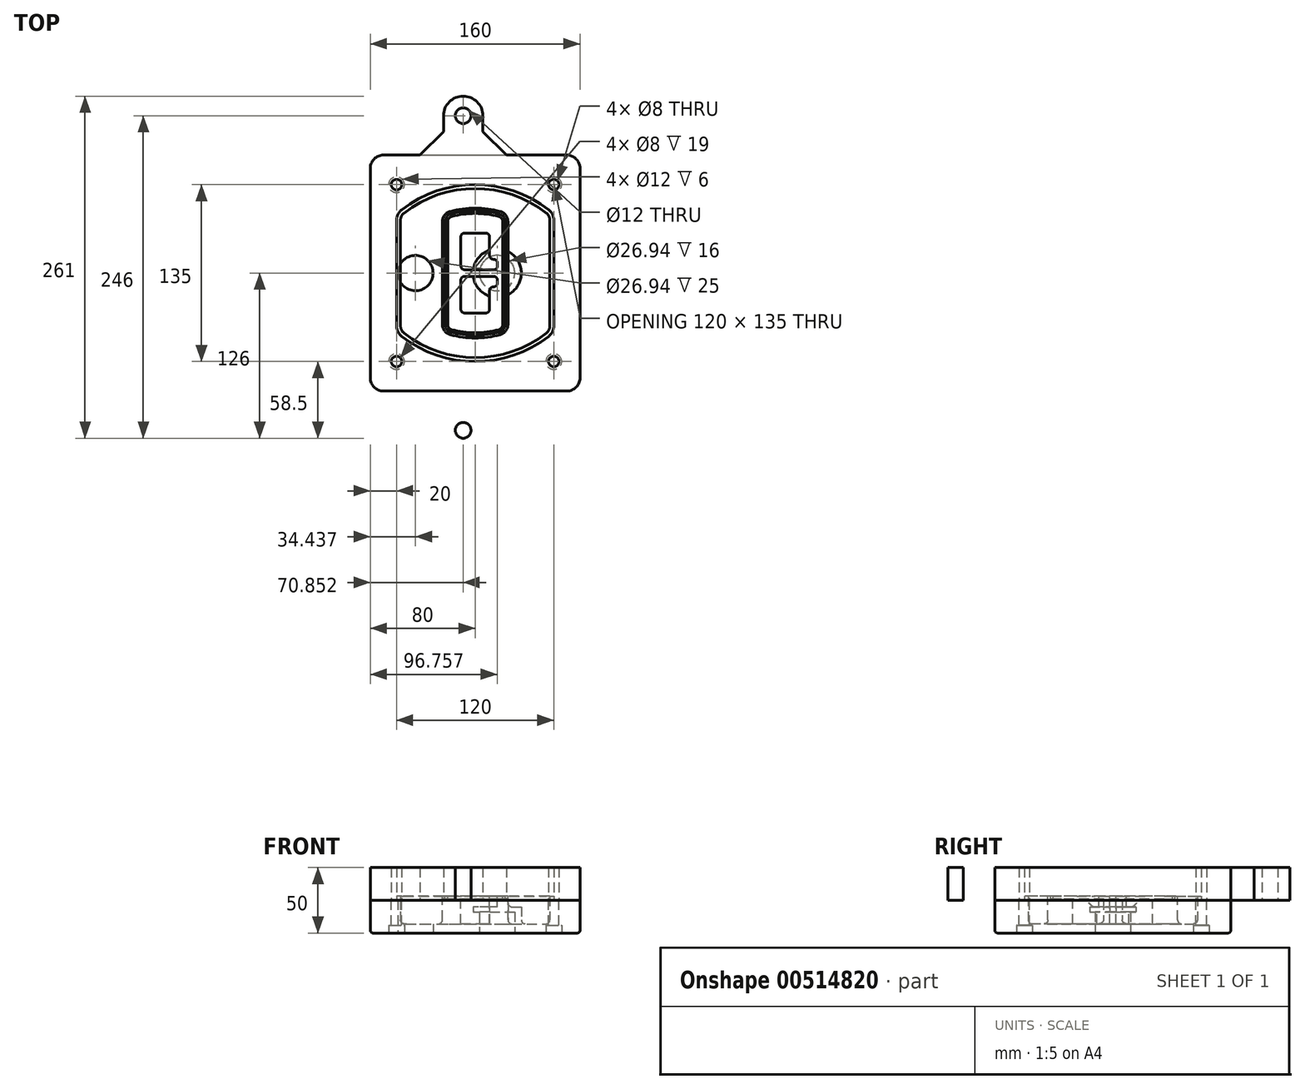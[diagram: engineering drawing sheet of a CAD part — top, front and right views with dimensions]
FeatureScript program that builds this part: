
annotation { "Feature Type Name" : "Feature", "Feature Type Description" : "" }
export const myFeature = defineFeature(function(context is Context, id is Id, definition is map)
    precondition{}
    {
        {
            var Q0;
            Q0=qCreatedBy(makeId("Top.planeOp"),FACE);
            var sketch = newSketch(context, id + "F0", { "sketchPlane" : qUnion([Q0])});
            skPoint(sketch, "E0.rect.middle", {"position": v(0, 0) * mm});
            skLineSegment(sketch, "E1.bottom", {"start": v(-70, -90) * mm, "end": v(70, -90) * mm});
            skLineSegment(sketch, "E1.top", {"start": v(-70, 90) * mm, "end": v(70, 90) * mm});
            skLineSegment(sketch, "E1.left", {"start": v(-80, -80) * mm, "end": v(-80, 80) * mm});
            skLineSegment(sketch, "E1.right", {"start": v(80, -80) * mm, "end": v(80, 80) * mm});
            skLineSegment(sketch, "E2", {"start": v(-80, 90) * mm, "end": v(80, -90) * mm, "construction": true});
            skLineSegment(sketch, "E3", {"start": v(80, 90) * mm, "end": v(-80, -90) * mm, "construction": true});
            skCircle(sketch, "E4", {"center": v(-60, 67.5) * mm, "radius": 4 * mm});
            skCircle(sketch, "E5", {"center": v(60, 67.5) * mm, "radius": 4 * mm});
            skCircle(sketch, "E6", {"center": v(60, -67.5) * mm, "radius": 4 * mm});
            skCircle(sketch, "E7", {"center": v(-60, -67.5) * mm, "radius": 4 * mm});
            skLineSegment(sketch, "E8", {"start": v(-60, 67.5) * mm, "end": v(60, 67.5) * mm, "construction": true});
            skLineSegment(sketch, "E9", {"start": v(60, 67.5) * mm, "end": v(60, -67.5) * mm, "construction": true});
            skLineSegment(sketch, "E10", {"start": v(60, -67.5) * mm, "end": v(-60, -67.5) * mm, "construction": true});
            skLineSegment(sketch, "E11", {"start": v(-60, -67.5) * mm, "end": v(-60, 67.5) * mm, "construction": true});
            skLineSegment(sketch, "E12", {"start": v(-60, 40.3) * mm, "end": v(-60, -40.3) * mm});
            skLineSegment(sketch, "E13", {"start": v(60, 40.3) * mm, "end": v(60, -40.3) * mm});
            skArc(sketch, "E14", {"start": v(56.15, 48.18) * mm, "mid": v(0, 67.5) * mm, "end": v(-56.15, 48.18) * mm});
            skArc(sketch, "E15", {"start": v(-56.15, -48.18) * mm, "mid": v(0, -67.5) * mm, "end": v(56.15, -48.18) * mm});
            skLineSegment(sketch, "E16", {"start": v(-60, 0) * mm, "end": v(60, 0) * mm, "construction": true});
            skPoint(sketch, "E17.visualSharp", {"position": v(-60, -45) * mm});
            skArc(sketch, "E17.filletArc", {"start": v(-60, -40.3) * mm, "mid": v(-58.99, -44.68) * mm, "end": v(-56.15, -48.18) * mm});
            skPoint(sketch, "E18.visualSharp", {"position": v(-60, 45) * mm});
            skArc(sketch, "E18.filletArc", {"start": v(-56.15, 48.18) * mm, "mid": v(-58.99, 44.68) * mm, "end": v(-60, 40.3) * mm});
            skPoint(sketch, "E19.visualSharp", {"position": v(60, 45) * mm});
            skArc(sketch, "E19.filletArc", {"start": v(60, 40.3) * mm, "mid": v(58.99, 44.68) * mm, "end": v(56.15, 48.18) * mm});
            skPoint(sketch, "E20.visualSharp", {"position": v(60, -45) * mm});
            skArc(sketch, "E20.filletArc", {"start": v(56.15, -48.18) * mm, "mid": v(58.99, -44.68) * mm, "end": v(60, -40.3) * mm});
            skPoint(sketch, "E21.visualSharp", {"position": v(-80, 90) * mm});
            skArc(sketch, "E21.filletArc", {"start": v(-70, 90) * mm, "mid": v(-77.07, 87.07) * mm, "end": v(-80, 80) * mm});
            skPoint(sketch, "E22.visualSharp", {"position": v(80, 90) * mm});
            skArc(sketch, "E22.filletArc", {"start": v(80, 80) * mm, "mid": v(77.07, 87.07) * mm, "end": v(70, 90) * mm});
            skPoint(sketch, "E23.visualSharp", {"position": v(80, -90) * mm});
            skArc(sketch, "E23.filletArc", {"start": v(70, -90) * mm, "mid": v(77.07, -87.07) * mm, "end": v(80, -80) * mm});
            skPoint(sketch, "E24.visualSharp", {"position": v(-80, -90) * mm});
            skArc(sketch, "E24.filletArc", {"start": v(-80, -80) * mm, "mid": v(-77.07, -87.07) * mm, "end": v(-70, -90) * mm});
            skArc(sketch, "E25.0", {"start": v(57, 40.3) * mm, "mid": v(56.3, 43.36) * mm, "end": v(54.3, 45.81) * mm});
            skLineSegment(sketch, "E25.1", {"start": v(57, 40.3) * mm, "end": v(57, -40.3) * mm});
            skArc(sketch, "E25.2", {"start": v(54.3, -45.81) * mm, "mid": v(56.3, -43.36) * mm, "end": v(57, -40.3) * mm});
            skArc(sketch, "E25.3", {"start": v(-54.3, -45.81) * mm, "mid": v(0, -64.5) * mm, "end": v(54.3, -45.81) * mm});
            skArc(sketch, "E25.4", {"start": v(-57, -40.3) * mm, "mid": v(-56.3, -43.36) * mm, "end": v(-54.3, -45.81) * mm});
            skArc(sketch, "E25.5", {"start": v(54.3, 45.81) * mm, "mid": v(0, 64.5) * mm, "end": v(-54.3, 45.81) * mm});
            skLineSegment(sketch, "E25.6", {"start": v(-57, 40.3) * mm, "end": v(-57, -40.3) * mm});
            skArc(sketch, "E25.7", {"start": v(-54.3, 45.81) * mm, "mid": v(-56.3, 43.36) * mm, "end": v(-57, 40.3) * mm});
            skArc(sketch, "E26.0", {"start": v(-58.62, 51.33) * mm, "mid": v(-62.58, 46.43) * mm, "end": v(-64, 40.3) * mm});
            skArc(sketch, "E26.1", {"start": v(58.62, 51.33) * mm, "mid": v(0, 71.5) * mm, "end": v(-58.62, 51.33) * mm});
            skArc(sketch, "E26.2", {"start": v(64, 40.3) * mm, "mid": v(62.58, 46.43) * mm, "end": v(58.62, 51.33) * mm});
            skLineSegment(sketch, "E26.3", {"start": v(64, 40.3) * mm, "end": v(64, -40.3) * mm});
            skArc(sketch, "E26.4", {"start": v(58.62, -51.33) * mm, "mid": v(62.58, -46.43) * mm, "end": v(64, -40.3) * mm});
            skLineSegment(sketch, "E26.5", {"start": v(-64, 40.3) * mm, "end": v(-64, -40.3) * mm});
            skArc(sketch, "E26.6", {"start": v(-58.62, -51.33) * mm, "mid": v(0, -71.5) * mm, "end": v(58.62, -51.33) * mm});
            skArc(sketch, "E26.7", {"start": v(-64, -40.3) * mm, "mid": v(-62.58, -46.43) * mm, "end": v(-58.62, -51.33) * mm});
            skSolve(sketch);
        }
        {
            var Q0;
            Q0=makeQuery(id+"F0.imprint","IMPRINT",FACE,{"disambiguationData":[TD([[makeQuery(id+"F0.imprint","IMPRINT",EDGE,{"derivedFrom":sQuery(id+"F0.wireOp",EDGE,"E1.bottom")}),1.0]])]});
            var Q1;
            Q1=makeQuery(id+"F0.imprint","IMPRINT",FACE,{"disambiguationData":[TD([[makeQuery(id+"F0.imprint","IMPRINT",EDGE,{"derivedFrom":sQuery(id+"F0.wireOp",EDGE,"E12")}),1.0]])]});
            var Q2;
            Q2=makeQuery(id+"F0.imprint","IMPRINT",FACE,{"disambiguationData":[TD([[makeQuery(id+"F0.imprint","IMPRINT",EDGE,{"derivedFrom":sQuery(id+"F0.wireOp",EDGE,"E25.0")}),1.0]])]});
            var Q3;
            Q3=makeQuery(id+"F0.imprint","IMPRINT",FACE,{"disambiguationData":[TD([[makeQuery(id+"F0.imprint","IMPRINT",EDGE,{"derivedFrom":sQuery(id+"F0.wireOp",EDGE,"E12")}),-1.0]])]});
            extrude(context, id + "F1", {"entities" : qUnion([Q0, Q1, Q2, Q3]), "oppositeDirection" : true, "depth" : 25 * mm});
        }
        {
            var Q0;
            Q0=makeQuery(id+"F0.imprint","IMPRINT",FACE,{"disambiguationData":[TD([[makeQuery(id+"F0.imprint","IMPRINT",EDGE,{"derivedFrom":sQuery(id+"F0.wireOp",EDGE,"E12")}),1.0]])]});
            extrude(context, id + "F2", {"entities" : qUnion([Q0]), "operationType" : NewBodyOperationType.ADD, "depth" : 3 * mm});
        }
        {
            var Q0;
            Q0=makeQuery(id+"F0.imprint","IMPRINT",FACE,{"disambiguationData":[TD([[makeQuery(id+"F0.imprint","IMPRINT",EDGE,{"derivedFrom":sQuery(id+"F0.wireOp",EDGE,"E25.0")}),1.0]])]});
            extrude(context, id + "F3", {"entities" : qUnion([Q0]), "operationType" : NewBodyOperationType.REMOVE, "oppositeDirection" : true, "depth" : 18 * mm});
        }
        {
            var Q0;
            Q0=makeQuery(id+"F2.opExtrude","CAP_FACE",FACE,{"disambiguationData":[OSD([sQuery(id+"F0.wireOp",EDGE,"E12"),sQuery(id+"F0.wireOp",EDGE,"E13"),sQuery(id+"F0.wireOp",EDGE,"E14"),sQuery(id+"F0.wireOp",EDGE,"E15"),sQuery(id+"F0.wireOp",EDGE,"E17.filletArc"),sQuery(id+"F0.wireOp",EDGE,"E18.filletArc"),sQuery(id+"F0.wireOp",EDGE,"E19.filletArc"),sQuery(id+"F0.wireOp",EDGE,"E20.filletArc"),sQuery(id+"F0.wireOp",EDGE,"E25.0"),sQuery(id+"F0.wireOp",EDGE,"E25.1"),sQuery(id+"F0.wireOp",EDGE,"E25.2"),sQuery(id+"F0.wireOp",EDGE,"E25.3"),sQuery(id+"F0.wireOp",EDGE,"E25.4"),sQuery(id+"F0.wireOp",EDGE,"E25.5"),sQuery(id+"F0.wireOp",EDGE,"E25.6"),sQuery(id+"F0.wireOp",EDGE,"E25.7")])],"isStart":false});
            var sketch = newSketch(context, id + "F4", { "sketchPlane" : qUnion([Q0])});
            skArc(sketch, "E27.0", {"start": v(-19.08, -46.97) * mm, "mid": v(0, -49.5) * mm, "end": v(19.08, -46.97) * mm});
            skArc(sketch, "E28.0", {"start": v(19.08, 46.97) * mm, "mid": v(0, 49.5) * mm, "end": v(-19.08, 46.97) * mm});
            skLineSegment(sketch, "E29", {"start": v(-25, 39.25) * mm, "end": v(-25, -39.25) * mm});
            skLineSegment(sketch, "E30", {"start": v(25, 39.25) * mm, "end": v(25, -39.25) * mm});
            skLineSegment(sketch, "E31", {"start": v(-25, 45.1) * mm, "end": v(25, 45.1) * mm, "construction": true});
            skLineSegment(sketch, "E32", {"start": v(-25, -45.1) * mm, "end": v(25, -45.1) * mm, "construction": true});
            skPoint(sketch, "E33.visualSharp", {"position": v(-25, 45.1) * mm});
            skArc(sketch, "E33.filletArc", {"start": v(-19.08, 46.97) * mm, "mid": v(-23.35, 44.11) * mm, "end": v(-25, 39.25) * mm});
            skPoint(sketch, "E34.visualSharp", {"position": v(25, 45.1) * mm});
            skArc(sketch, "E34.filletArc", {"start": v(25, 39.25) * mm, "mid": v(23.35, 44.11) * mm, "end": v(19.08, 46.97) * mm});
            skPoint(sketch, "E35.visualSharp", {"position": v(25, -45.1) * mm});
            skArc(sketch, "E35.filletArc", {"start": v(19.08, -46.97) * mm, "mid": v(23.35, -44.11) * mm, "end": v(25, -39.25) * mm});
            skPoint(sketch, "E36.visualSharp", {"position": v(-25, -45.1) * mm});
            skArc(sketch, "E36.filletArc", {"start": v(-25, -39.25) * mm, "mid": v(-23.35, -44.11) * mm, "end": v(-19.08, -46.97) * mm});
            skArc(sketch, "E37.0", {"start": v(54.3, 45.81) * mm, "mid": v(0, 64.5) * mm, "end": v(-54.3, 45.81) * mm});
            skArc(sketch, "E37.1", {"start": v(-54.3, 45.81) * mm, "mid": v(-56.3, 43.36) * mm, "end": v(-57, 40.3) * mm});
            skLineSegment(sketch, "E37.2", {"start": v(-57, 40.3) * mm, "end": v(-57, -40.3) * mm});
            skArc(sketch, "E37.3", {"start": v(-57, -40.3) * mm, "mid": v(-56.3, -43.36) * mm, "end": v(-54.3, -45.81) * mm});
            skArc(sketch, "E37.4", {"start": v(-54.3, -45.81) * mm, "mid": v(0, -64.5) * mm, "end": v(54.3, -45.81) * mm});
            skArc(sketch, "E37.5", {"start": v(54.3, -45.81) * mm, "mid": v(56.3, -43.36) * mm, "end": v(57, -40.3) * mm});
            skLineSegment(sketch, "E37.6", {"start": v(57, 40.3) * mm, "end": v(57, -40.3) * mm});
            skArc(sketch, "E37.7", {"start": v(57, 40.3) * mm, "mid": v(56.3, 43.36) * mm, "end": v(54.3, 45.81) * mm});
            skLineSegment(sketch, "E38.0", {"start": v(23, 39.25) * mm, "end": v(23, -39.25) * mm});
            skArc(sketch, "E38.1", {"start": v(18.56, -45.04) * mm, "mid": v(21.76, -42.9) * mm, "end": v(23, -39.25) * mm});
            skArc(sketch, "E38.2", {"start": v(-18.56, -45.04) * mm, "mid": v(0, -47.5) * mm, "end": v(18.56, -45.04) * mm});
            skArc(sketch, "E38.3", {"start": v(-23, -39.25) * mm, "mid": v(-21.76, -42.9) * mm, "end": v(-18.56, -45.04) * mm});
            skLineSegment(sketch, "E38.4", {"start": v(-23, 39.25) * mm, "end": v(-23, -39.25) * mm});
            skArc(sketch, "E38.5", {"start": v(23, 39.25) * mm, "mid": v(21.76, 42.9) * mm, "end": v(18.56, 45.04) * mm});
            skArc(sketch, "E38.6", {"start": v(-18.56, 45.04) * mm, "mid": v(-21.76, 42.9) * mm, "end": v(-23, 39.25) * mm});
            skArc(sketch, "E38.7", {"start": v(18.56, 45.04) * mm, "mid": v(0, 47.5) * mm, "end": v(-18.56, 45.04) * mm});
            skArc(sketch, "E39.0", {"start": v(21, 39.25) * mm, "mid": v(20.18, 41.68) * mm, "end": v(18.04, 43.1) * mm});
            skLineSegment(sketch, "E39.1", {"start": v(21, 39.25) * mm, "end": v(21, -39.25) * mm});
            skArc(sketch, "E39.2", {"start": v(18.04, -43.1) * mm, "mid": v(20.18, -41.68) * mm, "end": v(21, -39.25) * mm});
            skArc(sketch, "E39.3", {"start": v(-18.04, -43.1) * mm, "mid": v(0, -45.5) * mm, "end": v(18.04, -43.1) * mm});
            skArc(sketch, "E39.4", {"start": v(-21, -39.25) * mm, "mid": v(-20.18, -41.68) * mm, "end": v(-18.04, -43.1) * mm});
            skArc(sketch, "E39.5", {"start": v(18.04, 43.1) * mm, "mid": v(0, 45.5) * mm, "end": v(-18.04, 43.1) * mm});
            skLineSegment(sketch, "E39.6", {"start": v(-21, 39.25) * mm, "end": v(-21, -39.25) * mm});
            skArc(sketch, "E39.7", {"start": v(-18.04, 43.1) * mm, "mid": v(-20.18, 41.68) * mm, "end": v(-21, 39.25) * mm});
            skLineSegment(sketch, "E40", {"start": v(-25, 0) * mm, "end": v(25, 0) * mm, "construction": true});
            skLineSegment(sketch, "E41", {"start": v(-11, 5.5) * mm, "end": v(-11, 27.5) * mm});
            skLineSegment(sketch, "E42", {"start": v(-8, 30.5) * mm, "end": v(8, 30.5) * mm});
            skLineSegment(sketch, "E43", {"start": v(11, 27.5) * mm, "end": v(11, 13.5) * mm});
            skLineSegment(sketch, "E44", {"start": v(14, 10.5) * mm, "end": v(14, 10.5) * mm});
            skLineSegment(sketch, "E45", {"start": v(17, 7.5) * mm, "end": v(17, 5.5) * mm});
            skLineSegment(sketch, "E46", {"start": v(14, 2.5) * mm, "end": v(-8, 2.5) * mm});
            skPoint(sketch, "E47.visualSharp", {"position": v(-11, 30.5) * mm});
            skArc(sketch, "E47.filletArc", {"start": v(-8, 30.5) * mm, "mid": v(-10.12, 29.62) * mm, "end": v(-11, 27.5) * mm});
            skPoint(sketch, "E48.visualSharp", {"position": v(11, 30.5) * mm});
            skArc(sketch, "E48.filletArc", {"start": v(11, 27.5) * mm, "mid": v(10.12, 29.62) * mm, "end": v(8, 30.5) * mm});
            skPoint(sketch, "E49.visualSharp", {"position": v(11, 10.5) * mm});
            skArc(sketch, "E49.filletArc", {"start": v(11, 13.5) * mm, "mid": v(11.88, 11.38) * mm, "end": v(14, 10.5) * mm});
            skPoint(sketch, "E50.visualSharp", {"position": v(17, 10.5) * mm});
            skArc(sketch, "E50.filletArc", {"start": v(17, 7.5) * mm, "mid": v(16.12, 9.62) * mm, "end": v(14, 10.5) * mm});
            skPoint(sketch, "E51.visualSharp", {"position": v(17, 2.5) * mm});
            skArc(sketch, "E51.filletArc", {"start": v(14, 2.5) * mm, "mid": v(16.12, 3.38) * mm, "end": v(17, 5.5) * mm});
            skPoint(sketch, "E52.visualSharp", {"position": v(-11, 2.5) * mm});
            skArc(sketch, "E52.filletArc", {"start": v(-11, 5.5) * mm, "mid": v(-10.12, 3.38) * mm, "end": v(-8, 2.5) * mm});
            skLineSegment(sketch, "E53.0.MirrorCS", {"start": v(14, -2.5) * mm, "end": v(-8, -2.5) * mm});
            skArc(sketch, "E54.0.MirrorCS", {"start": v(-11, -5.5) * mm, "mid": v(-10.12, -3.38) * mm, "end": v(-8, -2.5) * mm});
            skLineSegment(sketch, "E55.0.MirrorCS", {"start": v(-11, -5.5) * mm, "end": v(-11, -27.5) * mm});
            skArc(sketch, "E56.0.MirrorCS", {"start": v(-8, -30.5) * mm, "mid": v(-10.12, -29.62) * mm, "end": v(-11, -27.5) * mm});
            skLineSegment(sketch, "E57.0.MirrorCS", {"start": v(-8, -30.5) * mm, "end": v(8, -30.5) * mm});
            skArc(sketch, "E58.0.MirrorCS", {"start": v(11, -27.5) * mm, "mid": v(10.12, -29.62) * mm, "end": v(8, -30.5) * mm});
            skLineSegment(sketch, "E59.0.MirrorCS", {"start": v(11, -27.5) * mm, "end": v(11, -13.5) * mm});
            skArc(sketch, "E60.0.MirrorCS", {"start": v(11, -13.5) * mm, "mid": v(11.88, -11.38) * mm, "end": v(14, -10.5) * mm});
            skArc(sketch, "E61.0.MirrorCS", {"start": v(17, -7.5) * mm, "mid": v(16.12, -9.62) * mm, "end": v(14, -10.5) * mm});
            skLineSegment(sketch, "E62.0.MirrorCS", {"start": v(17, -7.5) * mm, "end": v(17, -5.5) * mm});
            skArc(sketch, "E63.0.MirrorCS", {"start": v(14, -2.5) * mm, "mid": v(16.12, -3.38) * mm, "end": v(17, -5.5) * mm});
            skSolve(sketch);
        }
        {
            var Q0;
            Q0=makeQuery(id+"F4.imprint","IMPRINT",FACE,{"disambiguationData":[TD([[makeQuery(id+"F4.imprint","IMPRINT",EDGE,{"derivedFrom":sQuery(id+"F4.wireOp",EDGE,"E27.0")}),1.0]])]});
            var Q1;
            Q1=makeQuery(id+"F4.imprint","IMPRINT",FACE,{"disambiguationData":[TD([[makeQuery(id+"F4.imprint","IMPRINT",EDGE,{"derivedFrom":sQuery(id+"F4.wireOp",EDGE,"E38.0")}),-1.0]])]});
            var Q2;
            Q2=makeQuery(id+"F4.imprint","IMPRINT",FACE,{"disambiguationData":[TD([[makeQuery(id+"F4.imprint","IMPRINT",EDGE,{"derivedFrom":sQuery(id+"F4.wireOp",EDGE,"E39.0")}),1.0]])]});
            extrude(context, id + "F5", {"entities" : qUnion([Q0, Q1, Q2]), "operationType" : NewBodyOperationType.ADD, "endBound" : BoundingType.UP_TO_NEXT, "oppositeDirection" : true, "depth" : 25 * mm});
        }
        {
            var Q0;
            Q0=makeQuery(id+"F4.imprint","IMPRINT",FACE,{"disambiguationData":[TD([[makeQuery(id+"F4.imprint","IMPRINT",EDGE,{"derivedFrom":sQuery(id+"F4.wireOp",EDGE,"E38.0")}),-1.0]])]});
            extrude(context, id + "F6", {"entities" : qUnion([Q0]), "operationType" : NewBodyOperationType.REMOVE, "oppositeDirection" : true, "depth" : 2 * mm});
        }
        {
            var Q0;
            Q0=makeQuery(id+"F1.opExtrude","CAP_FACE",FACE,{"disambiguationData":[OSD([sQuery(id+"F0.wireOp",EDGE,"E1.bottom"),sQuery(id+"F0.wireOp",EDGE,"E1.top"),sQuery(id+"F0.wireOp",EDGE,"E1.left"),sQuery(id+"F0.wireOp",EDGE,"E1.right"),sQuery(id+"F0.wireOp",EDGE,"E4"),sQuery(id+"F0.wireOp",EDGE,"E5"),sQuery(id+"F0.wireOp",EDGE,"E6"),sQuery(id+"F0.wireOp",EDGE,"E7"),sQuery(id+"F0.wireOp",EDGE,"E21.filletArc"),sQuery(id+"F0.wireOp",EDGE,"E22.filletArc"),sQuery(id+"F0.wireOp",EDGE,"E23.filletArc"),sQuery(id+"F0.wireOp",EDGE,"E24.filletArc")])],"isStart":false});
            var sketch = newSketch(context, id + "F7", { "sketchPlane" : qUnion([Q0])});
            skCircle(sketch, "E64", {"center": v(16.76, 0) * mm, "radius": 13.47 * mm});
            skCircle(sketch, "E65", {"center": v(-45.56, 0) * mm, "radius": 13.47 * mm});
            skLineSegment(sketch, "E66", {"start": v(80, 0) * mm, "end": v(-80, 0) * mm});
            skCircle(sketch, "E67", {"center": v(16.76, 0) * mm, "radius": 18.47 * mm});
            skCircle(sketch, "E68", {"center": v(60, -67.5) * mm, "radius": 6 * mm});
            skCircle(sketch, "E69", {"center": v(-60, -67.5) * mm, "radius": 6 * mm});
            skCircle(sketch, "E70", {"center": v(-60, 67.5) * mm, "radius": 6 * mm});
            skCircle(sketch, "E71", {"center": v(60, 67.5) * mm, "radius": 6 * mm});
            skSolve(sketch);
        }
        {
            var Q0;
            {var subQ1=sQuery(id+"F7.wireOp",EDGE,"E66");var subQ4=sQuery(id+"F7.wireOp",EDGE,"E64");var subQ6=makeQuery(id+"F7.imprint","INTERSECT",VERTEX,{"disambiguationData":[OD(0.0)],"derivedFrom":[subQ4,subQ1]});Q0=makeQuery(id+"F7.imprint","IMPRINT",FACE,{"disambiguationData":[TD([[makeQuery(id+"F7.imprint","IMPRINT",EDGE,{"disambiguationData":[TD([[subQ6,-1.0]])],"derivedFrom":subQ4}),-1.0]])]});}
            var Q1;
            {var subQ0=sQuery(id+"F7.wireOp",EDGE,"E66");var subQ1=sQuery(id+"F7.wireOp",EDGE,"E64");var subQ3=makeQuery(id+"F7.imprint","INTERSECT",VERTEX,{"disambiguationData":[OD(0.0)],"derivedFrom":[subQ1,subQ0]});Q1=makeQuery(id+"F7.imprint","IMPRINT",FACE,{"disambiguationData":[TD([[makeQuery(id+"F7.imprint","IMPRINT",EDGE,{"disambiguationData":[TD([[subQ3,-1.0]])],"derivedFrom":subQ1}),1.0]])]});}
            var Q2;
            {var subQ0=sQuery(id+"F7.wireOp",EDGE,"E66");var subQ1=sQuery(id+"F7.wireOp",EDGE,"E64");var subQ3=makeQuery(id+"F7.imprint","INTERSECT",VERTEX,{"disambiguationData":[OD(0.0)],"derivedFrom":[subQ1,subQ0]});Q2=makeQuery(id+"F7.imprint","IMPRINT",FACE,{"disambiguationData":[TD([[makeQuery(id+"F7.imprint","IMPRINT",EDGE,{"disambiguationData":[TD([[subQ3,1.0]])],"derivedFrom":subQ1}),1.0]])]});}
            var Q3;
            {var subQ1=sQuery(id+"F7.wireOp",EDGE,"E66");var subQ4=sQuery(id+"F7.wireOp",EDGE,"E64");var subQ6=makeQuery(id+"F7.imprint","INTERSECT",VERTEX,{"disambiguationData":[OD(0.0)],"derivedFrom":[subQ4,subQ1]});Q3=makeQuery(id+"F7.imprint","IMPRINT",FACE,{"disambiguationData":[TD([[makeQuery(id+"F7.imprint","IMPRINT",EDGE,{"disambiguationData":[TD([[subQ6,1.0]])],"derivedFrom":subQ4}),-1.0]])]});}
            extrude(context, id + "F8", {"entities" : qUnion([Q0, Q1, Q2, Q3]), "operationType" : NewBodyOperationType.ADD, "oppositeDirection" : true, "depth" : 20 * mm});
        }
        {
            var Q0;
            {var subQ0=sQuery(id+"F7.wireOp",EDGE,"E66");var subQ1=sQuery(id+"F7.wireOp",EDGE,"E64");var subQ3=makeQuery(id+"F7.imprint","INTERSECT",VERTEX,{"disambiguationData":[OD(0.0)],"derivedFrom":[subQ1,subQ0]});Q0=makeQuery(id+"F7.imprint","IMPRINT",FACE,{"disambiguationData":[TD([[makeQuery(id+"F7.imprint","IMPRINT",EDGE,{"disambiguationData":[TD([[subQ3,-1.0]])],"derivedFrom":subQ1}),1.0]])]});}
            var Q1;
            {var subQ0=sQuery(id+"F7.wireOp",EDGE,"E66");var subQ1=sQuery(id+"F7.wireOp",EDGE,"E64");var subQ3=makeQuery(id+"F7.imprint","INTERSECT",VERTEX,{"disambiguationData":[OD(0.0)],"derivedFrom":[subQ1,subQ0]});Q1=makeQuery(id+"F7.imprint","IMPRINT",FACE,{"disambiguationData":[TD([[makeQuery(id+"F7.imprint","IMPRINT",EDGE,{"disambiguationData":[TD([[subQ3,1.0]])],"derivedFrom":subQ1}),1.0]])]});}
            extrude(context, id + "F9", {"entities" : qUnion([Q0, Q1]), "operationType" : NewBodyOperationType.REMOVE, "oppositeDirection" : true, "depth" : 16 * mm});
        }
        {
            var Q0;
            {var subQ0=sQuery(id+"F7.wireOp",EDGE,"E66");var subQ1=sQuery(id+"F7.wireOp",EDGE,"E65");var subQ3=makeQuery(id+"F7.imprint","INTERSECT",VERTEX,{"disambiguationData":[OD(0.0)],"derivedFrom":[subQ1,subQ0]});Q0=makeQuery(id+"F7.imprint","IMPRINT",FACE,{"disambiguationData":[TD([[makeQuery(id+"F7.imprint","IMPRINT",EDGE,{"disambiguationData":[TD([[subQ3,-1.0]])],"derivedFrom":subQ1}),1.0]])]});}
            var Q1;
            {var subQ0=sQuery(id+"F7.wireOp",EDGE,"E66");var subQ1=sQuery(id+"F7.wireOp",EDGE,"E65");var subQ3=makeQuery(id+"F7.imprint","INTERSECT",VERTEX,{"disambiguationData":[OD(0.0)],"derivedFrom":[subQ1,subQ0]});Q1=makeQuery(id+"F7.imprint","IMPRINT",FACE,{"disambiguationData":[TD([[makeQuery(id+"F7.imprint","IMPRINT",EDGE,{"disambiguationData":[TD([[subQ3,1.0]])],"derivedFrom":subQ1}),1.0]])]});}
            extrude(context, id + "F10", {"entities" : qUnion([Q0, Q1]), "operationType" : NewBodyOperationType.REMOVE, "oppositeDirection" : true, "depth" : 25 * mm});
        }
        {
            var Q0;
            Q0=makeQuery(id+"F7.imprint","IMPRINT",FACE,{"disambiguationData":[TD([[makeQuery(id+"F7.imprint","IMPRINT",EDGE,{"derivedFrom":sQuery(id+"F7.wireOp",EDGE,"E68")}),1.0]])]});
            var Q1;
            Q1=makeQuery(id+"F7.imprint","IMPRINT",FACE,{"disambiguationData":[TD([[makeQuery(id+"F7.imprint","IMPRINT",EDGE,{"derivedFrom":makeQuery(id+"F1.opExtrude","CAP_EDGE",EDGE,{"disambiguationData":[OSD([sQuery(id+"F0.wireOp",EDGE,"E5")])],"isStart":false})}),-1.0]])]});
            var Q2;
            Q2=makeQuery(id+"F7.imprint","IMPRINT",FACE,{"disambiguationData":[TD([[makeQuery(id+"F7.imprint","IMPRINT",EDGE,{"derivedFrom":sQuery(id+"F7.wireOp",EDGE,"E69")}),1.0]])]});
            var Q3;
            Q3=makeQuery(id+"F7.imprint","IMPRINT",FACE,{"disambiguationData":[TD([[makeQuery(id+"F7.imprint","IMPRINT",EDGE,{"derivedFrom":makeQuery(id+"F1.opExtrude","CAP_EDGE",EDGE,{"disambiguationData":[OSD([sQuery(id+"F0.wireOp",EDGE,"E4")])],"isStart":false})}),-1.0]])]});
            var Q4;
            Q4=makeQuery(id+"F7.imprint","IMPRINT",FACE,{"disambiguationData":[TD([[makeQuery(id+"F7.imprint","IMPRINT",EDGE,{"derivedFrom":sQuery(id+"F7.wireOp",EDGE,"E70")}),1.0]])]});
            var Q5;
            Q5=makeQuery(id+"F7.imprint","IMPRINT",FACE,{"disambiguationData":[TD([[makeQuery(id+"F7.imprint","IMPRINT",EDGE,{"derivedFrom":makeQuery(id+"F1.opExtrude","CAP_EDGE",EDGE,{"disambiguationData":[OSD([sQuery(id+"F0.wireOp",EDGE,"E7")])],"isStart":false})}),-1.0]])]});
            var Q6;
            Q6=makeQuery(id+"F7.imprint","IMPRINT",FACE,{"disambiguationData":[TD([[makeQuery(id+"F7.imprint","IMPRINT",EDGE,{"derivedFrom":sQuery(id+"F7.wireOp",EDGE,"E71")}),1.0]])]});
            var Q7;
            Q7=makeQuery(id+"F7.imprint","IMPRINT",FACE,{"disambiguationData":[TD([[makeQuery(id+"F7.imprint","IMPRINT",EDGE,{"derivedFrom":makeQuery(id+"F1.opExtrude","CAP_EDGE",EDGE,{"disambiguationData":[OSD([sQuery(id+"F0.wireOp",EDGE,"E6")])],"isStart":false})}),-1.0]])]});
            extrude(context, id + "F11", {"entities" : qUnion([Q0, Q1, Q2, Q3, Q4, Q5, Q6, Q7]), "operationType" : NewBodyOperationType.REMOVE, "oppositeDirection" : true, "depth" : 6 * mm});
        }
        {
            var Q0;
            Q0=makeQuery(id+"F9.boolean.opBoolean","COPY",FACE,{"derivedFrom":makeQuery(id+"F9.opExtrude","CAP_FACE",FACE,{"disambiguationData":[OSD([sQuery(id+"F7.wireOp",EDGE,"E64")])],"isStart":false})});
            var sketch = newSketch(context, id + "F12", { "sketchPlane" : qUnion([Q0])});
            skArc(sketch, "E72.0", {"start": v(11, 17.55) * mm, "mid": v(2.57, 11.82) * mm, "end": v(-1.54, 2.5) * mm});
            skArc(sketch, "E72.1", {"start": v(-1.54, -2.5) * mm, "mid": v(2.57, -11.82) * mm, "end": v(11, -17.55) * mm});
            skLineSegment(sketch, "E73", {"start": v(-1.54, -2.5) * mm, "end": v(14, -2.5) * mm});
            skLineSegment(sketch, "E74.0", {"start": v(14, 2.5) * mm, "end": v(-1.54, 2.5) * mm});
            skArc(sketch, "E74.1", {"start": v(14, 2.5) * mm, "mid": v(16.12, 3.38) * mm, "end": v(17, 5.5) * mm});
            skLineSegment(sketch, "E74.2", {"start": v(17, 7.5) * mm, "end": v(17, 5.5) * mm});
            skArc(sketch, "E74.3", {"start": v(17, 7.5) * mm, "mid": v(16.12, 9.62) * mm, "end": v(14, 10.5) * mm});
            skArc(sketch, "E74.4", {"start": v(11, 13.5) * mm, "mid": v(11.88, 11.38) * mm, "end": v(14, 10.5) * mm});
            skLineSegment(sketch, "E74.5", {"start": v(11, 17.55) * mm, "end": v(11, 13.5) * mm});
            skLineSegment(sketch, "E74.7", {"start": v(14, -2.5) * mm, "end": v(-1.54, -2.5) * mm});
            skArc(sketch, "E74.8", {"start": v(14, -2.5) * mm, "mid": v(16.12, -3.38) * mm, "end": v(17, -5.5) * mm});
            skLineSegment(sketch, "E74.9", {"start": v(17, -7.5) * mm, "end": v(17, -5.5) * mm});
            skArc(sketch, "E74.10", {"start": v(17, -7.5) * mm, "mid": v(16.12, -9.62) * mm, "end": v(14, -10.5) * mm});
            skArc(sketch, "E74.11", {"start": v(11, -13.5) * mm, "mid": v(11.88, -11.38) * mm, "end": v(14, -10.5) * mm});
            skLineSegment(sketch, "E74.12", {"start": v(11, -17.55) * mm, "end": v(11, -13.5) * mm});
            skPoint(sketch, "E75.orphan", {"position": v(11, -27.5) * mm});
            skPoint(sketch, "E76.orphan", {"position": v(-8, -2.5) * mm});
            skPoint(sketch, "E77.orphan", {"position": v(-8, 2.5) * mm});
            skPoint(sketch, "E78.orphan", {"position": v(11, 27.5) * mm});
            skSolve(sketch);
        }
        {
            var Q0;
            {var subQ7=sQuery(id+"F12.wireOp",EDGE,"E72.0");var subQ14=sQuery(id+"F12.wireOp",EDGE,"E72.1");var subQ16=sQuery(id+"F12.wireOp",EDGE,"E74.1");var subQ18=sQuery(id+"F12.wireOp",EDGE,"E74.8");Q0=qUnion([makeQuery(id+"F12.imprint","IMPRINT",FACE,{"disambiguationData":[TD([[makeQuery(id+"F12.imprint","IMPRINT",EDGE,{"derivedFrom":subQ7}),1.0]])]}),makeQuery(id+"F12.imprint","IMPRINT",FACE,{"disambiguationData":[TD([[makeQuery(id+"F12.imprint","IMPRINT",EDGE,{"derivedFrom":subQ14}),1.0]])]}),makeQuery(id+"F12.imprint","IMPRINT",FACE,{"disambiguationData":[TD([[makeQuery(id+"F12.imprint","IMPRINT",EDGE,{"derivedFrom":subQ16}),1.0]])]}),makeQuery(id+"F12.imprint","IMPRINT",FACE,{"disambiguationData":[TD([[makeQuery(id+"F12.imprint","IMPRINT",EDGE,{"derivedFrom":subQ18}),-1.0]])]})]);}
            var Q1;
            Q1=makeQuery(id+"F5.boolean.opBoolean","SPLIT",FACE,{"disambiguationData":[TD([makeQuery(id+"F5.opExtrude","SWEPT_FACE",FACE,{"disambiguationData":[OSD([sQuery(id+"F4.wireOp",EDGE,"E41")])]})])],"derivedFrom":makeQuery(id+"F3.boolean.opBoolean","COPY",FACE,{"derivedFrom":makeQuery(id+"F3.opExtrude","CAP_FACE",FACE,{"disambiguationData":[OSD([sQuery(id+"F0.wireOp",EDGE,"E25.0"),sQuery(id+"F0.wireOp",EDGE,"E25.1"),sQuery(id+"F0.wireOp",EDGE,"E25.2"),sQuery(id+"F0.wireOp",EDGE,"E25.3"),sQuery(id+"F0.wireOp",EDGE,"E25.4"),sQuery(id+"F0.wireOp",EDGE,"E25.5"),sQuery(id+"F0.wireOp",EDGE,"E25.6"),sQuery(id+"F0.wireOp",EDGE,"E25.7")])],"isStart":false})})});
            extrude(context, id + "F13", {"entities" : qUnion([Q0]), "operationType" : NewBodyOperationType.REMOVE, "endBound" : BoundingType.UP_TO_SURFACE, "endBoundEntityFace" : qUnion([Q1]), "depth" : 25 * mm});
        }
        {
            var Q0;
            Q0=makeQuery(id+"F3.boolean.opBoolean","COPY",EDGE,{"derivedFrom":makeQuery(id+"F3.opExtrude","CAP_EDGE",EDGE,{"disambiguationData":[OSD([sQuery(id+"F0.wireOp",EDGE,"E25.6")])],"isStart":false})});
            var Q1;
            Q1=makeQuery(id+"F8.boolean.opBoolean","INTERSECT",EDGE,{"derivedFrom":[makeQuery(id+"F5.opExtrude","SWEPT_FACE",FACE,{"disambiguationData":[OSD([sQuery(id+"F4.wireOp",EDGE,"E30")])]}),makeQuery(id+"F8.opExtrude","CAP_FACE",FACE,{"disambiguationData":[OSD([sQuery(id+"F7.wireOp",EDGE,"E67")])],"isStart":false})]});
            var Q2;
            Q2=makeQuery(id+"F8.boolean.opBoolean","INTERSECT",EDGE,{"disambiguationData":[OD(1.0)],"derivedFrom":[makeQuery(id+"F5.opExtrude","SWEPT_FACE",FACE,{"disambiguationData":[OSD([sQuery(id+"F4.wireOp",EDGE,"E30")])]}),makeQuery(id+"F8.opExtrude","SWEPT_FACE",FACE,{"disambiguationData":[OSD([sQuery(id+"F7.wireOp",EDGE,"E67")])]})]});
            var Q3;
            {var subQ0=sQuery(id+"F4.wireOp",EDGE,"E30");Q3=makeQuery(id+"F8.boolean.opBoolean","SPLIT",EDGE,{"disambiguationData":[TD([makeQuery(id+"F5.opExtrude","SWEPT_FACE",FACE,{"disambiguationData":[OSD([sQuery(id+"F4.wireOp",EDGE,"E35.filletArc")])]})])],"derivedFrom":makeQuery(id+"F5.opExtrude","CAP_EDGE",EDGE,{"disambiguationData":[OSD([subQ0])],"isStart":false})});}
            var Q4;
            {var subQ0=sQuery(id+"F0.wireOp",EDGE,"E25.7");var subQ1=sQuery(id+"F0.wireOp",EDGE,"E25.1");var subQ2=sQuery(id+"F0.wireOp",EDGE,"E25.6");var subQ3=sQuery(id+"F0.wireOp",EDGE,"E25.5");var subQ4=sQuery(id+"F0.wireOp",EDGE,"E25.4");var subQ5=sQuery(id+"F0.wireOp",EDGE,"E25.0");var subQ6=sQuery(id+"F0.wireOp",EDGE,"E25.2");var subQ7=sQuery(id+"F0.wireOp",EDGE,"E25.3");Q4=makeQuery(id+"F8.boolean.opBoolean","INTERSECT",EDGE,{"derivedFrom":[makeQuery(id+"F5.boolean.opBoolean","SPLIT",FACE,{"disambiguationData":[TD([makeQuery(id+"F2.opExtrude","SWEPT_FACE",FACE,{"disambiguationData":[OSD([subQ5])]})])],"derivedFrom":makeQuery(id+"F3.boolean.opBoolean","COPY",FACE,{"derivedFrom":makeQuery(id+"F3.opExtrude","CAP_FACE",FACE,{"disambiguationData":[OSD([subQ5,subQ1,subQ6,subQ7,subQ4,subQ3,subQ2,subQ0])],"isStart":false})})}),makeQuery(id+"F8.opExtrude","SWEPT_FACE",FACE,{"disambiguationData":[OSD([sQuery(id+"F7.wireOp",EDGE,"E67")])]})]});}
            var Q5;
            Q5=makeQuery(id+"F8.boolean.opBoolean","INTERSECT",EDGE,{"disambiguationData":[OD(0.0)],"derivedFrom":[makeQuery(id+"F5.opExtrude","SWEPT_FACE",FACE,{"disambiguationData":[OSD([sQuery(id+"F4.wireOp",EDGE,"E30")])]}),makeQuery(id+"F8.opExtrude","SWEPT_FACE",FACE,{"disambiguationData":[OSD([sQuery(id+"F7.wireOp",EDGE,"E67")])]})]});
            fillet(context, id + "F14", {"entities" : qUnion([Q0, Q1, Q2, Q3, Q4, Q5]), "radius" : 3 * mm, "tangentPropagation" : true, "allowEdgeOverflow" : false});
        }
        {
            var Q0;
            Q0=makeQuery(id+"F1.opExtrude","CAP_EDGE",EDGE,{"disambiguationData":[OSD([sQuery(id+"F0.wireOp",EDGE,"E1.bottom")])],"isStart":false});
            fillet(context, id + "F15", {"entities" : qUnion([Q0]), "radius" : 2 * mm, "tangentPropagation" : true, "allowEdgeOverflow" : false});
        }
        {
            var Q0;
            {var subQ0=sQuery(id+"F0.wireOp",EDGE,"E21.filletArc");var subQ1=sQuery(id+"F0.wireOp",EDGE,"E7");var subQ2=sQuery(id+"F0.wireOp",EDGE,"E6");var subQ3=sQuery(id+"F0.wireOp",EDGE,"E5");var subQ4=sQuery(id+"F0.wireOp",EDGE,"E4");var subQ5=sQuery(id+"F0.wireOp",EDGE,"E22.filletArc");var subQ6=sQuery(id+"F0.wireOp",EDGE,"E1.bottom");var subQ7=sQuery(id+"F0.wireOp",EDGE,"E1.right");var subQ8=sQuery(id+"F0.wireOp",EDGE,"E1.top");var subQ9=sQuery(id+"F0.wireOp",EDGE,"E1.left");var subQ10=sQuery(id+"F0.wireOp",EDGE,"E23.filletArc");var subQ11=sQuery(id+"F0.wireOp",EDGE,"E24.filletArc");Q0=makeQuery(id+"F2.boolean.opBoolean","SPLIT",FACE,{"disambiguationData":[TD([makeQuery(id+"F1.opExtrude","SWEPT_FACE",FACE,{"disambiguationData":[OSD([subQ6])]})])],"derivedFrom":makeQuery(id+"F1.opExtrude","CAP_FACE",FACE,{"disambiguationData":[OSD([subQ6,subQ8,subQ9,subQ7,subQ4,subQ3,subQ2,subQ1,subQ0,subQ5,subQ10,subQ11])],"isStart":true})});}
            var sketch = newSketch(context, id + "F16", { "sketchPlane" : qUnion([Q0])});
            skLineSegment(sketch, "E79.0", {"start": v(-80, -80) * mm, "end": v(-80, 80) * mm});
            skLineSegment(sketch, "E79.1", {"start": v(-60, 40.3) * mm, "end": v(-60, -40.3) * mm});
            skArc(sketch, "E79.2", {"start": v(-56.15, -48.18) * mm, "mid": v(0, -67.5) * mm, "end": v(56.15, -48.18) * mm});
            skArc(sketch, "E79.3", {"start": v(-60, -40.3) * mm, "mid": v(-58.99, -44.68) * mm, "end": v(-56.15, -48.18) * mm});
            skArc(sketch, "E79.4", {"start": v(-56.15, 48.18) * mm, "mid": v(-58.99, 44.68) * mm, "end": v(-60, 40.3) * mm});
            skArc(sketch, "E79.5", {"start": v(56.15, 48.18) * mm, "mid": v(0, 67.5) * mm, "end": v(-56.15, 48.18) * mm});
            skArc(sketch, "E79.6", {"start": v(60, 40.3) * mm, "mid": v(58.99, 44.68) * mm, "end": v(56.15, 48.18) * mm});
            skLineSegment(sketch, "E79.7", {"start": v(60, 40.3) * mm, "end": v(60, -40.3) * mm});
            skArc(sketch, "E79.8", {"start": v(56.15, -48.18) * mm, "mid": v(58.99, -44.68) * mm, "end": v(60, -40.3) * mm});
            skArc(sketch, "E79.9", {"start": v(-70, 90) * mm, "mid": v(-77.07, 87.07) * mm, "end": v(-80, 80) * mm});
            skLineSegment(sketch, "E79.10", {"start": v(-70, 90) * mm, "end": v(70, 90) * mm});
            skArc(sketch, "E79.11", {"start": v(80, 80) * mm, "mid": v(77.07, 87.07) * mm, "end": v(70, 90) * mm});
            skLineSegment(sketch, "E79.12", {"start": v(80, -80) * mm, "end": v(80, 80) * mm});
            skArc(sketch, "E79.13", {"start": v(70, -90) * mm, "mid": v(77.07, -87.07) * mm, "end": v(80, -80) * mm});
            skLineSegment(sketch, "E79.14", {"start": v(-70, -90) * mm, "end": v(70, -90) * mm});
            skArc(sketch, "E79.15", {"start": v(-80, -80) * mm, "mid": v(-77.07, -87.07) * mm, "end": v(-70, -90) * mm});
            skCircle(sketch, "E79.16", {"center": v(-60, 67.5) * mm, "radius": 4 * mm});
            skCircle(sketch, "E79.17", {"center": v(60, 67.5) * mm, "radius": 4 * mm});
            skCircle(sketch, "E79.18", {"center": v(60, -67.5) * mm, "radius": 4 * mm});
            skCircle(sketch, "E79.19", {"center": v(-60, -67.5) * mm, "radius": 4 * mm});
            skLineSegment(sketch, "E80", {"start": v(-42.15, 90) * mm, "end": v(-24.15, 108) * mm});
            skLineSegment(sketch, "E81", {"start": v(-24.15, 108) * mm, "end": v(-24.15, 120) * mm});
            skLineSegment(sketch, "E82", {"start": v(23.85, 90) * mm, "end": v(5.85, 108) * mm});
            skLineSegment(sketch, "E83", {"start": v(5.85, 108) * mm, "end": v(5.85, 120) * mm});
            skArc(sketch, "E84", {"start": v(5.85, 120) * mm, "mid": v(-9.15, 135) * mm, "end": v(-24.15, 120) * mm});
            skCircle(sketch, "E85", {"center": v(-9.15, 120) * mm, "radius": 6 * mm});
            skLineSegment(sketch, "E86", {"start": v(-9.15, 120) * mm, "end": v(-9.15, 90) * mm, "construction": true});
            skLineSegment(sketch, "E87", {"start": v(-80, 0) * mm, "end": v(80, 0) * mm, "construction": true});
            skLineSegment(sketch, "E88.MirrorCS", {"start": v(-12.15, 123) * mm, "end": v(-42.15, 123) * mm, "construction": true});
            skLineSegment(sketch, "E89.MirrorCS", {"start": v(-24.15, 108) * mm, "end": v(-12.15, 108) * mm});
            skLineSegment(sketch, "E90.MirrorCS", {"start": v(-9.15, -120) * mm, "end": v(-9.15, -90) * mm, "construction": true});
            skCircle(sketch, "E91.MirrorC", {"center": v(-9.15, -120) * mm, "radius": 6 * mm});
            skLineSegment(sketch, "E92.MirrorCS", {"start": v(-42.15, -90) * mm, "end": v(-24.15, -108) * mm});
            skArc(sketch, "E93.MirrorCS", {"start": v(5.85, -120) * mm, "mid": v(-9.15, -135) * mm, "end": v(-24.15, -120) * mm});
            skLineSegment(sketch, "E94.MirrorCS", {"start": v(-24.15, -108) * mm, "end": v(-24.15, -120) * mm});
            skLineSegment(sketch, "E95.MirrorCS", {"start": v(23.85, -90) * mm, "end": v(5.85, -108) * mm});
            skLineSegment(sketch, "E96.MirrorCS", {"start": v(5.85, -108) * mm, "end": v(5.85, -120) * mm});
            skLineSegment(sketch, "E97.MirrorCS", {"start": v(-24.15, 92.25) * mm, "end": v(-12.15, 92.25) * mm});
            skSolve(sketch);
        }
        {
            var Q0;
            Q0=makeQuery(id+"F16.imprint","IMPRINT",FACE,{"disambiguationData":[TD([[makeQuery(id+"F16.imprint","IMPRINT",EDGE,{"derivedFrom":sQuery(id+"F16.wireOp",EDGE,"E79.0")}),-1.0]])]});
            var Q1;
            {var subQ1=sQuery(id+"F16.wireOp",EDGE,"E80");Q1=makeQuery(id+"F16.imprint","IMPRINT",FACE,{"disambiguationData":[TD([[makeQuery(id+"F16.imprint","IMPRINT",EDGE,{"derivedFrom":subQ1}),-1.0]])]});}
            var Q2;
            Q2=makeQuery(id+"F16.imprint","IMPRINT",FACE,{"disambiguationData":[TD([[makeQuery(id+"F16.imprint","IMPRINT",EDGE,{"derivedFrom":sQuery(id+"F16.wireOp",EDGE,"E91.MirrorC")}),1.0]])]});
            extrude(context, id + "F17", {"entities" : qUnion([Q0, Q1, Q2]), "depth" : 25 * mm});
        }
    });
